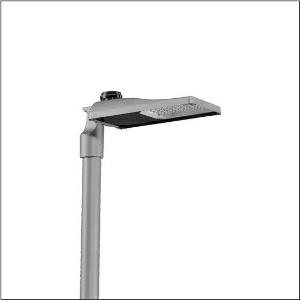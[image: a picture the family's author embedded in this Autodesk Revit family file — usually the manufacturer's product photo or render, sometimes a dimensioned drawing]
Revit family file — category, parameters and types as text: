
# Revit family: streetlight_sl_31_mini___st1_0a_5xh6d3bn08ga_df69
name_source: partatom
category: Lighting Fixtures
units: mm (PartAtom-declared; Revit-internal decimal feet)

## family parameters
Cut with Voids When Loaded = No
Host = Face
Light Source = No
Part Type = Normal
Room Calculation Point = No
Round Connector Dimension = Use Diameter
Shared = No

## types (1)
- --- (1 x LED, 5710 lm, 37.3 W, 3000K)
    Apparent Load = 37 VA
    CIE Flux Codes = 37 72 97 100 100
    Color Rendering = 70
    Color Temperature = 3000K
    Default Elevation = 1800 mm
    Description = Streetlight SL 31 mini NEMA (7pin) mast luminaire for post-top, side-entry; light control with lens of PMMA; light distribution: ST1.0a, direct asymmetric distribution, for standard-compliant lighting for roads and squares; LED: luminous flux: 5.710lm, light colour: 730, colour temperature: 3000K; luminous efficacy: 153,1lm/W; control: pre-setting: linear dimming characteristic, flexible luminous flux parameterisation, time-dependent luminous flux control, constant luminous flux control, intelligent temperature release in ECG and LED module, overheat protection; luminaire housing, of diecast aluminium, SITECO metallic grey (DB 702S), corrosivity category C5 high according to DIN EN ISO 12944; cover of toughened safety glass, transparent, opened without tools; mast flange of diecast aluminium, SITECO metallic grey (DB 702S), spigot size: 76/60mm, mast flange included unmounted; cable length: 6,5m, connection cable pre-assembled; mains connection: 220..240V, AC, 50/60Hz; power consumption (at start of service life): 37,3W / (at end of service life): 38,7W / (with reduced operation 50%): 17,5W; protection rating (complete): IP66; insulation class (complete): insulation class I (protective earthing); impact resistance: IK10; certification: CE, ENEC, ENEC+, VDE, UKCA; permissible operating ambient temperature for outdoor applications: -40..+50°C; packaging unit: 1 piece

Light Distribution: ST1.0a
    Height = 76 mm
    Lamp = 1 x LED
    Lamp Light Flux = 5710 lm
    Lamp Power = 37.3 W
    Lamp count = 1
    Length = 547 mm
    Luminous efficacy = 153 lm/W
    Manufacturer = Siteco
    ModVariant = No
    Model = 5XH6D3BN08GA
    Number of Poles = 1
    OnlyDefault = Yes
    Power Factor = 1
    Product Name = Streetlight SL 31 mini | ST1.0a
    Product group = mast luminaire | pylon top
    ProductGroupID = 6100
    Protection Class = Protection class I
    Protection Degree = IP 66
    RLX_Detail_Level = 1
    RLX_Emergency_Light_Flux = 0 lm
    RLX_Emergency_Type = 0
    RLX_Emergency_Type_DB = No
    RlxData = <blob elided: 40229 chars, md5=227c0772>
    Socket = socket
    Standby Power = 0 W
    System Light Flux = 5710 lm
    System Power = 37 W
    Type Comments = factory setting: luminous flux: 100 % | dim-lin: 254 | 386 mA
    Type Image = l_1300322.jpg
    URL = http://relux.com
    VarID = @adj_060505
    Voltage = 0 V
    Weight = 0.00 kg
    Width = 265 mm

## geometry (parser evidence)
native form markers: Blend x4, Sweep x10
no freeform markers — native parametric forms only
